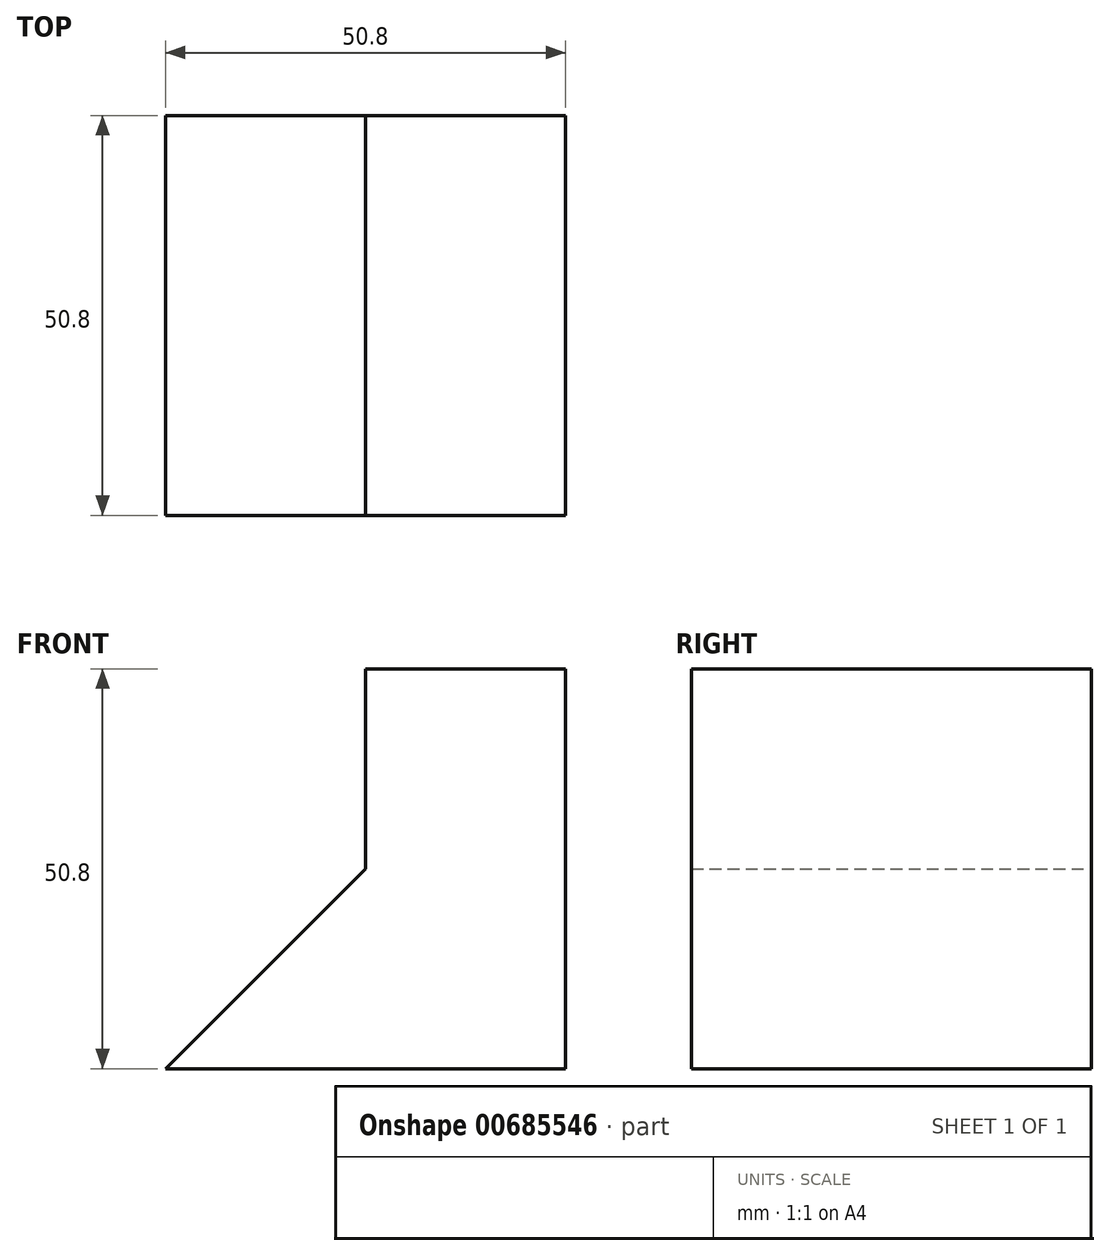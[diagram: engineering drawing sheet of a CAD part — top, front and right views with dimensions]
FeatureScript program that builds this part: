
annotation { "Feature Type Name" : "Feature", "Feature Type Description" : "" }
export const myFeature = defineFeature(function(context is Context, id is Id, definition is map)
    precondition{}
    {
        {
            var Q0;
            Q0=qCreatedBy(makeId("Front.planeOp"),FACE);
            var sketch = newSketch(context, id + "F0", { "sketchPlane" : qUnion([Q0])});
            skLineSegment(sketch, "E0", {"start": v(0, 0) * mm, "end": v(0, 50.8) * mm});
            skLineSegment(sketch, "E1", {"start": v(0, 50.8) * mm, "end": v(-25.4, 50.8) * mm});
            skLineSegment(sketch, "E2", {"start": v(-25.4, 50.8) * mm, "end": v(-25.4, 25.4) * mm});
            skLineSegment(sketch, "E3", {"start": v(0, 0) * mm, "end": v(-50.8, 0) * mm});
            skLineSegment(sketch, "E4", {"start": v(-50.8, 0) * mm, "end": v(-25.4, 25.4) * mm});
            skSolve(sketch);
        }
        {
            var Q0;
            Q0 = qSketchRegion(id + "F0", true);
            extrude(context, id + "F1", {"entities" : qUnion([Q0]), "depth" : 50.8 * mm, "offsetDistance" : 25.4 * mm});
        }
    });
